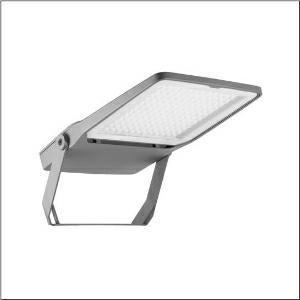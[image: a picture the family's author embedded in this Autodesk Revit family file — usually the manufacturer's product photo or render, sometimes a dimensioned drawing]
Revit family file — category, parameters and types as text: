
# Revit family: floodlight_fl_20_midi___pl61_5xa7682e3c1ac_6cc9
name_source: partatom
category: Lighting Fixtures
units: mm (PartAtom-declared; Revit-internal decimal feet)

## family parameters
Cut with Voids When Loaded = No
Host = Face
Light Source = No
Part Type = Normal
Room Calculation Point = No
Round Connector Dimension = Use Diameter
Shared = No

## types (1)
- --- (1 x LED 5000K / CRI = 70 (unbekannt), 27570 lm, 5000K)
    Apparent Load = 208 VA
    CIE Flux Codes = 33 65 98 100 100
    Color Rendering = 70
    Color Temperature = 5000K
    Default Elevation = 1800 mm
    Description = Floodlight FL 20 midi, floodlight, primary light control with lens, of plastic, primary optical cover: protective disc, of toughened safety glass, transparent, light distribution: PL61, light emission: direct distribution, primary light characteristic: asymmetric, installation type: surface-mounted, LED High Power LED, rated luminous flux: 27.570 lm, light colour: 750, colour temperature: 5000K, control gear: ECG Plus, control: flexible luminous flux parameterisation, time-dependent luminous flux control, digital communication interface, power reduction, overheat protection, electronic power reduction, with terminal, 5-pole, max. 2.5mm², mains connection: 220..240V, AC, 50/60Hz, rated input power: 208W, LED unit, of diecast aluminium, powder-coated, Siteco® metallic grey (DB 702S), length: 654 mm, width: 450 mm, height: 76mm, housing frame, of diecast aluminium, powder-coated, Siteco® metallic grey (DB 702S), mounting bracket, of steel, powder-coated, Siteco® metallic grey (DB 702S), DALIprotection rating (complete): IP66, insulation class (complete): insulation class II (safety insulation), certification: CE, ENEC, VDE, protection symbol: D, permissible ambient temperature for indoor applications: -40..+40°C, permissible ambient temperature for outdoor applications: -40..+50°C, standard: DIN EN 12944, packaging unit: 1 piece

Light Distribution: PL61
    Height = 76 mm
    Lamp = 1 x LED 5000K / CRI >= 70 (unbekannt)
    Lamp Light Flux = 27570 lm
    Lamp count = 1
    Length = 672 mm
    Luminous efficacy = 133 lm/W
    Manufacturer = Siteco
    ModVariant = No
    Model = 5XA7682E3C1AC
    Number of Poles = 1
    OnlyDefault = Yes
    Power Factor = 1
    Product Name = Floodlight FL 20 midi | PL61
    Product group = floodlight | pylon top
    ProductGroupID = 6101
    Protection Class = Protection class II
    Protection Degree = IP 66
    RLX_Detail_Level = 1
    RlxData = <blob elided: 98033 chars, md5=f16491f8>
    Socket = socket
    Standby Power = 0 W
    System Light Flux = 27570 lm
    System Power = 208 W
    Type Comments = factory setting: luminous flux: 100 % | dim-lin: 254 | 484 mA
    Type Image = l_1005943.jpg
    URL = http://relux.com
    VarID = @adj_142209
    Voltage = 0 V
    Weight = 0.00 kg
    Width = 450 mm

## geometry (parser evidence)
native form markers: Blend x4, Sweep x11
no freeform markers — native parametric forms only
